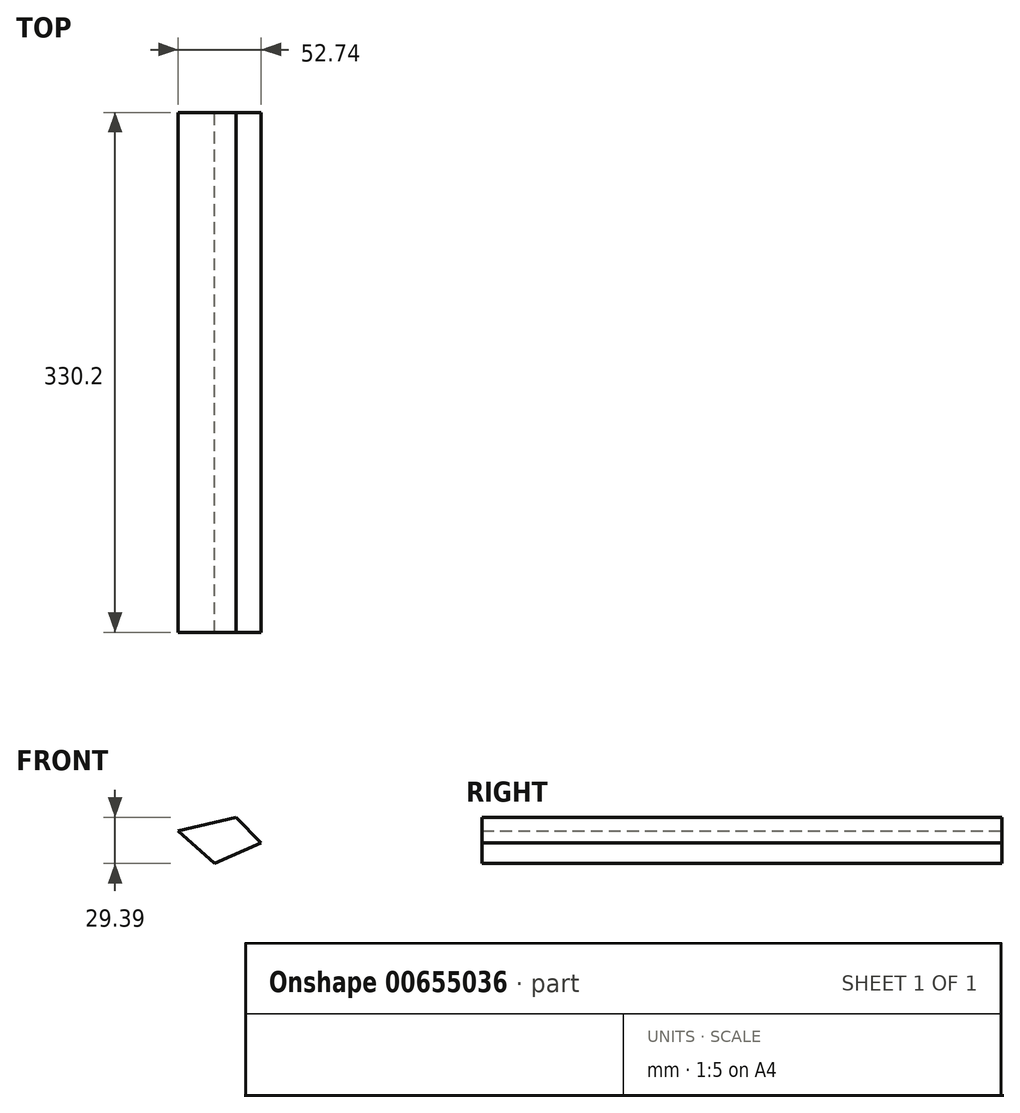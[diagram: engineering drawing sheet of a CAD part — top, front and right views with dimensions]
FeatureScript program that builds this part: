
annotation { "Feature Type Name" : "Feature", "Feature Type Description" : "" }
export const myFeature = defineFeature(function(context is Context, id is Id, definition is map)
    precondition{}
    {
        {
            var Q0;
            Q0=qCreatedBy(makeId("Front.planeOp"),FACE);
            var sketch = newSketch(context, id + "F0", { "sketchPlane" : qUnion([Q0])});
            skLineSegment(sketch, "E0", {"start": v(-71.64, 49.58) * mm, "end": v(-34.83, 58.19) * mm});
            skLineSegment(sketch, "E1", {"start": v(-18.9, 42.06) * mm, "end": v(-48.52, 28.8) * mm});
            skLineSegment(sketch, "E2", {"start": v(-48.52, 28.8) * mm, "end": v(-71.64, 49.58) * mm});
            skLineSegment(sketch, "E3", {"start": v(-34.83, 58.19) * mm, "end": v(-18.9, 42.06) * mm});
            skSolve(sketch);
        }
        {
            var Q0;
            Q0 = qSketchRegion(id + "F0", true);
            var Q1;
            Q1=makeQuery(id+"F0.imprint","IMPRINT",FACE,{"disambiguationData":[TD([[makeQuery(id+"F0.imprint","IMPRINT",EDGE,{"derivedFrom":sQuery(id+"F0.wireOp",EDGE,"E0")}),-1.0]])]});
            extrude(context, id + "F1", {"entities" : qUnion([Q0, Q1]), "depth" : 330.2 * mm, "offsetDistance" : 25.4 * mm});
        }
    });
